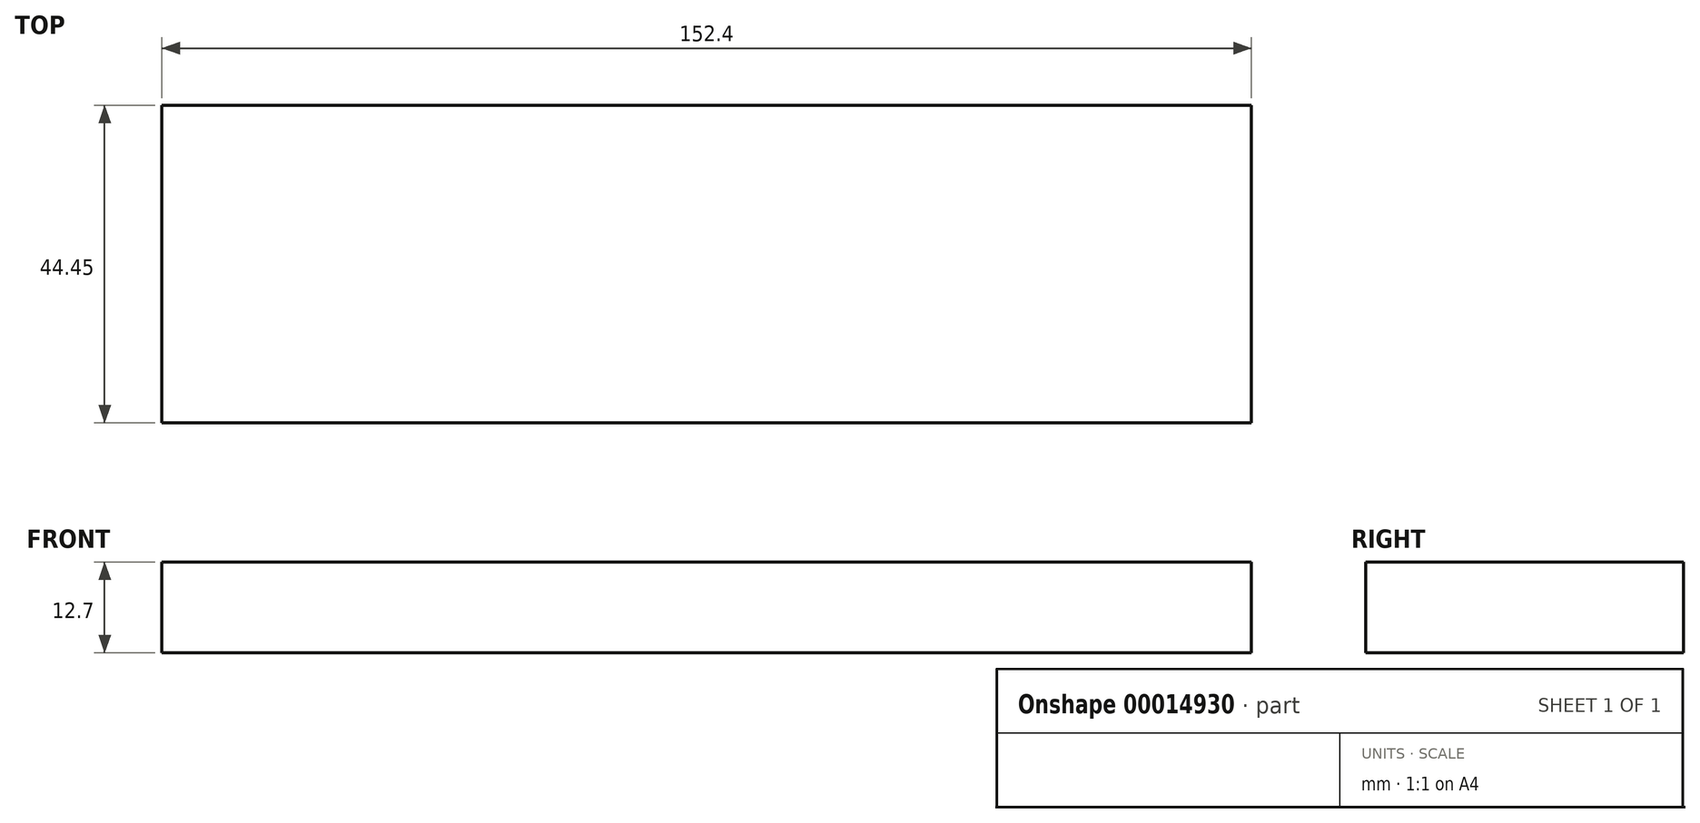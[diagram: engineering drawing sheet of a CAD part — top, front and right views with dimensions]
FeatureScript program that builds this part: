
annotation { "Feature Type Name" : "Feature", "Feature Type Description" : "" }
export const myFeature = defineFeature(function(context is Context, id is Id, definition is map)
    precondition{}
    {
        {
            var Q0;
            Q0=qCreatedBy(makeId("Top.planeOp"),FACE);
            var sketch = newSketch(context, id + "F0", { "sketchPlane" : qUnion([Q0])});
            skLineSegment(sketch, "E0.bottom", {"start": v(-57.23, 12.26) * mm, "end": v(95.17, 12.26) * mm});
            skLineSegment(sketch, "E0.top", {"start": v(-57.23, -32.19) * mm, "end": v(95.17, -32.19) * mm});
            skLineSegment(sketch, "E0.left", {"start": v(-57.23, 12.26) * mm, "end": v(-57.23, -32.19) * mm});
            skLineSegment(sketch, "E0.right", {"start": v(95.17, 12.26) * mm, "end": v(95.17, -32.19) * mm});
            skSolve(sketch);
        }
        {
            var Q0;
            Q0=makeQuery(id+"F0.imprint","IMPRINT",FACE,{"disambiguationData":[TD([[makeQuery(id+"F0.imprint","IMPRINT",EDGE,{"derivedFrom":sQuery(id+"F0.wireOp",EDGE,"E0.bottom")}),-1.0]])]});
            extrude(context, id + "F1", {"entities" : qUnion([Q0]), "depth" : 12.7 * mm});
        }
    });
